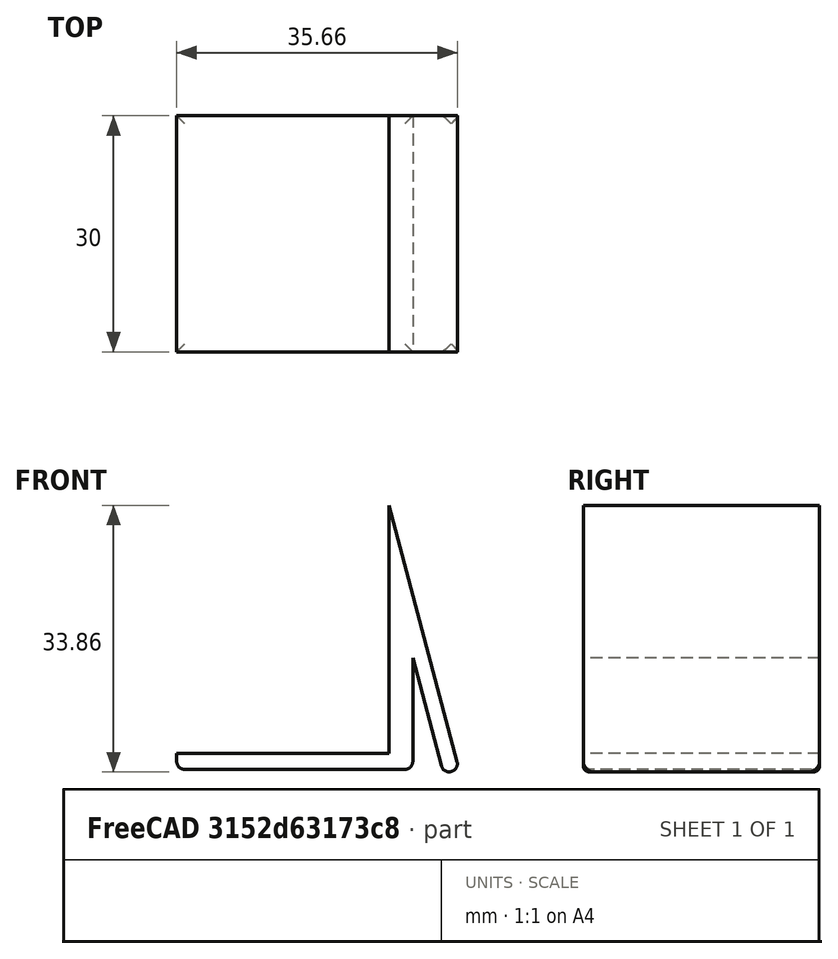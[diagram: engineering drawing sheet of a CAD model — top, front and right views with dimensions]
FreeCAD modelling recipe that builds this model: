
FCSTD DOCUMENT  (FreeCAD 2024.409R38991 (Git))
Label: TerraceFloorPegsSaw
License: All rights reserved
LicenseURL: https://en.wikipedia.org/wiki/All_rights_reserved
objects: Sketcher::SketchObject×1, PartDesign::Pad×1, PartDesign::Fillet×1, PartDesign::Body×1
note: 9 computed .brp shape members not serialized (recipe doc carries the construction recipe); baked Part::Feature solids carry a one-line shape summary decoded from their .brp

FEATURE [Sketcher::SketchObject] Sketch
  ArcFitTolerance = 1e-06
  AttachmentSupport = -> [XZ_Plane]
  ExternalBSplineMaxDegree = 5
  ExternalBSplineTolerance = 0.0001
  FullyConstrained = false
  InternalTolerance = 1e-06
  InvalidShape = false
  MakeInternals = false
  MapMode = 5
  Placement = pos=(0,0,0) rot=(1,0,0;1.5708rad)
  Support = -> [XZ_Plane]
  TreeRank = 11
  ValidateShape = false
  sketch-geometry (27):
    g0: LineSegment StartX=-0.104875 StartY=0 StartZ=0 EndX=-30.1049 EndY=0 EndZ=0
    g1: LineSegment StartX=-30.1049 StartY=0 StartZ=0 EndX=-30.1049 EndY=2 EndZ=0
    g2: LineSegment StartX=-30.1049 StartY=2 StartZ=0 EndX=-3.10487 EndY=2 EndZ=0
    g3: LineSegment StartX=-3.10487 StartY=2 StartZ=0 EndX=-3.10487 EndY=33.5444 EndZ=0
    g4: LineSegment StartX=-3.10487 StartY=33.5444 StartZ=0 EndX=5.78429 EndY=-0.013605 EndZ=0
    g5: LineSegment StartX=3.64395 StartY=-0.013605 StartZ=0 EndX=-0.104875 EndY=14.1388 EndZ=0
    g6: LineSegment StartX=-0.104875 StartY=14.1388 StartZ=0 EndX=-0.104875 EndY=0 EndZ=0
    g7: LineSegment [constr] StartX=-3.10487 StartY=2 StartZ=0 EndX=-0.104875 EndY=2 EndZ=0
    g8: LineSegment StartX=5.78429 StartY=-0.013605 StartZ=0 EndX=3.64395 EndY=-0.013605 EndZ=0
    g9: LineSegment StartX=-3.10487 StartY=2 StartZ=0 EndX=-3.68169 EndY=2.51127 EndZ=0
    g10: LineSegment StartX=-3.68169 StartY=2.51127 StartZ=0 EndX=-3.10487 EndY=2.97722 EndZ=0
    g11: LineSegment StartX=-3.10487 StartY=2.97722 StartZ=0 EndX=-3.65716 EndY=3.38595 EndZ=0
    g12: LineSegment StartX=-3.65716 StartY=3.38595 StartZ=0 EndX=-3.10487 EndY=3.8846 EndZ=0
    g13: LineSegment StartX=-3.10487 StartY=3.8846 StartZ=0 EndX=-3.61629 EndY=4.24428 EndZ=0
    g14: LineSegment StartX=-3.61629 StartY=4.24428 StartZ=0 EndX=-3.10487 EndY=4.62849 EndZ=0
    g15: LineSegment StartX=-3.10487 StartY=4.62849 StartZ=0 EndX=-3.59994 EndY=5.00452 EndZ=0
    g16: LineSegment StartX=-3.59994 StartY=5.00452 StartZ=0 EndX=-3.10487 EndY=5.29063 EndZ=0
    g17: LineSegment StartX=-3.10487 StartY=5.29063 StartZ=0 EndX=-3.58359 EndY=5.59309 EndZ=0
    g18: LineSegment StartX=-3.58359 StartY=5.59309 StartZ=0 EndX=-3.10487 EndY=5.89555 EndZ=0
    g19: LineSegment StartX=-3.10487 StartY=5.89555 StartZ=0 EndX=-3.58359 EndY=6.25523 EndZ=0
    g20: LineSegment StartX=-3.58359 StartY=6.25523 StartZ=0 EndX=-3.10487 EndY=6.50865 EndZ=0
    g21: LineSegment StartX=-3.10487 StartY=6.50865 StartZ=0 EndX=-3.64081 EndY=6.72936 EndZ=0
    g22: LineSegment StartX=-3.64081 StartY=6.72936 StartZ=0 EndX=-3.10487 EndY=6.93373 EndZ=0
    g23: LineSegment StartX=-3.10487 StartY=6.93373 StartZ=0 EndX=-3.63688 EndY=7.19492 EndZ=0
    g24: LineSegment StartX=-3.63688 StartY=7.19492 StartZ=0 EndX=-3.10487 EndY=7.61707 EndZ=0
    g25: LineSegment StartX=-3.10487 StartY=7.61707 StartZ=0 EndX=-3.66502 EndY=7.94073 EndZ=0
    g26: LineSegment StartX=-3.66502 StartY=7.94073 StartZ=0 EndX=-3.10487 EndY=8.26438 EndZ=0
  constraints (49):
    c: PointOnObject(g0,g-1)
    c: Horizontal(g0)
    c: Coincident(g0,g1)
    c: Coincident(g1,g2)
    c: Horizontal(g2)
    c: Coincident(g2,g3)
    c: Vertical(g3)
    c: Coincident(g3,g4)
    c: Coincident(g5,g6)
    c: Coincident(g6,g0)
    c: DistanceX(g0,g0) = 30
    c: Parallel(g6,g3)
    c: DistanceY(g1,g1) = 2
    c: Parallel(g5,g4)
    c: Coincident(g7,g2)
    c: PointOnObject(g7,g6)
    c: Horizontal(g7)
    c: DistanceX(g7,g7) = 3
    c: Angle(g0,g1) = 1.5708
    c: Coincident(g8,g4)
    c: Horizontal(g8)
    c: Coincident(g5,g8)
    c: Coincident(g2,g9)
    c: Coincident(g9,g10)
    c: PointOnObject(g10,g3)
    c: Coincident(g10,g11)
    c: Coincident(g11,g12)
    c: PointOnObject(g12,g3)
    c: Coincident(g12,g13)
    c: Coincident(g13,g14)
    c: PointOnObject(g14,g3)
    c: Coincident(g14,g15)
    c: Coincident(g15,g16)
    c: PointOnObject(g16,g3)
    c: Coincident(g16,g17)
    c: Coincident(g17,g18)
    c: PointOnObject(g18,g3)
    c: Coincident(g18,g19)
    c: Coincident(g19,g20)
    c: PointOnObject(g20,g3)
    c: Coincident(g20,g21)
    c: Coincident(g21,g22)
    c: PointOnObject(g22,g3)
    c: Coincident(g22,g23)
    c: Coincident(g23,g24)
    c: PointOnObject(g24,g3)
    c: Coincident(g24,g25)
    c: Coincident(g25,g26)
    c: PointOnObject(g26,g3)
FEATURE [PartDesign::Pad] Pad
  AddSubType = 0
  AlongSketchNormal = false
  AutoTaperInnerAngle = true
  CheckUpToFaceLimits = true
  ClaimChildren = false
  Direction = (0,-1,-2e-16)
  Fit = 0
  FitJoin = 0
  InnerFit = 0
  InnerFitJoin = 0
  InvalidShape = false
  Length = 20
  Length2 = 10
  Linearize = true
  NewSolid = false
  Profile = -> Sketch
  ReferenceAxis = -> Sketch [N_Axis]
  Suppress = false
  TaperInnerAngle = 0
  TaperInnerAngleRev = 0
  TreeRank = 12
  Type = 0
  ValidateShape = true
  _ProfileBasedVersion = 1
FEATURE [PartDesign::Fillet] Fillet
  AddSubType = 0
  Base = -> Pad [Edge2,Edge4,Edge3,Edge1,?Edge19,?Edge17,Edge20,?Edge18]
  BaseFeature = -> Pad
  InvalidShape = false
  NewSolid = false
  Radius = 1
  SupportTransform = false
  Suppress = false
  TreeRank = 13
  UseAllEdges = false
  ValidateShape = true
FEATURE [PartDesign::Body] Body
  AutoGroupSolids = false
  ClaimAllChildren = false
  ExportMode = 0
  Group = -> [Sketch,Pad,Fillet]
  InvalidShape = false
  Origin = -> Origin
  Tip = -> Fillet
  TreeRank = 10
  ValidateShape = false
  _ExportChildren = -> [Pad,Fillet]
  _GroupVersion = 1
